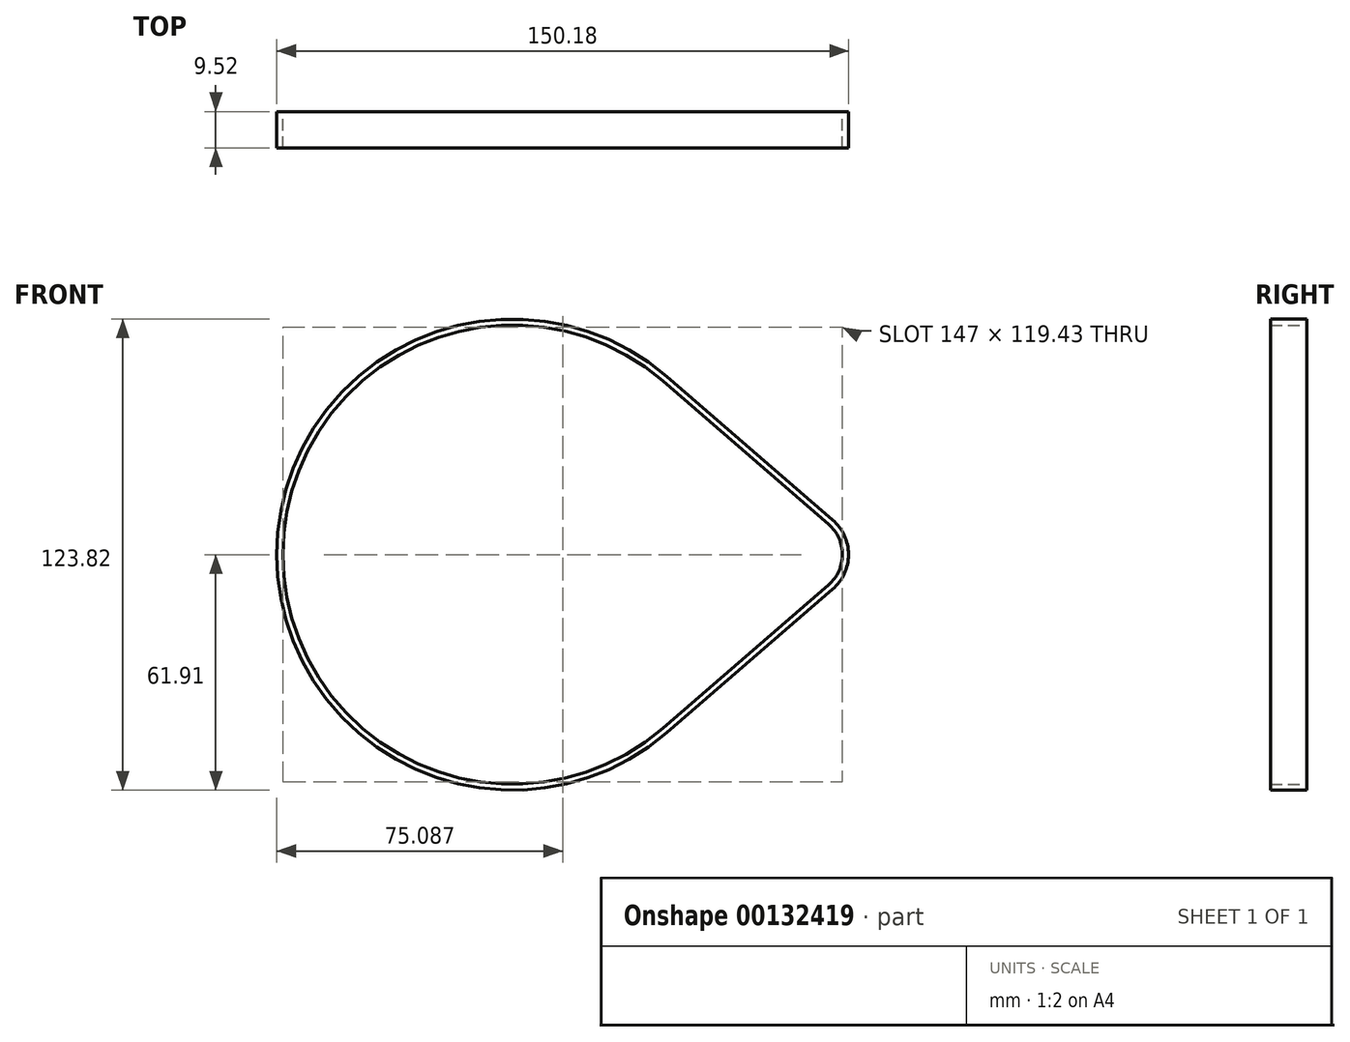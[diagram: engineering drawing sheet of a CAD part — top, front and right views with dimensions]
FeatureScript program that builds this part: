
annotation { "Feature Type Name" : "Feature", "Feature Type Description" : "" }
export const myFeature = defineFeature(function(context is Context, id is Id, definition is map)
    precondition{}
    {
        {
            var Q0;
            Q0=qCreatedBy(makeId("Front.planeOp"),FACE);
            var sketch = newSketch(context, id + "F0", { "sketchPlane" : qUnion([Q0])});
            skArc(sketch, "E0", {"start": v(39.46, 45.63) * mm, "mid": v(-60.33, 0) * mm, "end": v(39.46, -45.63) * mm});
            skArc(sketch, "E1", {"start": v(83.06, -7.93) * mm, "mid": v(86.68, 0) * mm, "end": v(83.06, 7.93) * mm});
            skLineSegment(sketch, "E2", {"start": v(39.46, 45.63) * mm, "end": v(83.06, 7.93) * mm});
            skLineSegment(sketch, "E3", {"start": v(39.46, -45.63) * mm, "end": v(83.06, -7.93) * mm});
            skLineSegment(sketch, "E4.0", {"start": v(40.5, 46.83) * mm, "end": v(84.1, 9.13) * mm});
            skArc(sketch, "E4.1", {"start": v(40.5, 46.83) * mm, "mid": v(-61.91, 0) * mm, "end": v(40.5, -46.83) * mm});
            skLineSegment(sketch, "E4.2", {"start": v(40.5, -46.83) * mm, "end": v(84.1, -9.13) * mm});
            skArc(sketch, "E4.3", {"start": v(84.1, -9.13) * mm, "mid": v(88.27, 0) * mm, "end": v(84.1, 9.13) * mm});
            skSolve(sketch);
        }
        {
            var Q0;
            Q0=makeQuery(id+"F0.imprint","IMPRINT",FACE,{"disambiguationData":[TD([[makeQuery(id+"F0.imprint","IMPRINT",EDGE,{"derivedFrom":sQuery(id+"F0.wireOp",EDGE,"E0")}),-1.0]])]});
            extrude(context, id + "F1", {"entities" : qUnion([Q0]), "endBound" : BoundingType.SYMMETRIC, "depth" : 9.52 * mm});
        }
    });
